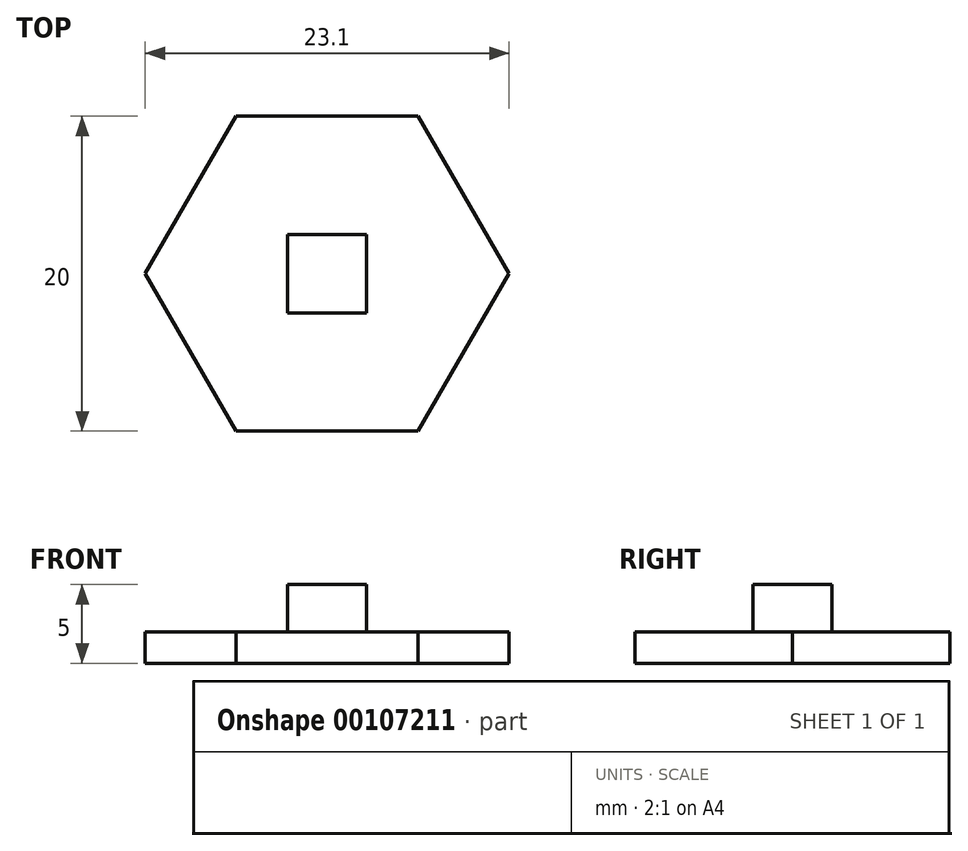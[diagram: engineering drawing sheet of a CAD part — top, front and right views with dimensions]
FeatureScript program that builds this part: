
annotation { "Feature Type Name" : "Feature", "Feature Type Description" : "" }
export const myFeature = defineFeature(function(context is Context, id is Id, definition is map)
    precondition{}
    {
        {
            var Q0;
            Q0=qCreatedBy(makeId("Top.planeOp"),FACE);
            var sketch = newSketch(context, id + "F0", { "sketchPlane" : qUnion([Q0])});
            skCircle(sketch, "E0.cCircle", {"center": v(0, 0) * mm, "radius": 10 * mm, "construction": true});
            skLineSegment(sketch, "E0.0", {"start": v(-5.77, 10) * mm, "end": v(5.77, 10) * mm});
            skLineSegment(sketch, "E0.1", {"start": v(5.77, 10) * mm, "end": v(11.55, 0) * mm});
            skLineSegment(sketch, "E0.2", {"start": v(11.55, 0) * mm, "end": v(5.77, -10) * mm});
            skLineSegment(sketch, "E0.3", {"start": v(5.77, -10) * mm, "end": v(-5.77, -10) * mm});
            skLineSegment(sketch, "E0.4", {"start": v(-5.77, -10) * mm, "end": v(-11.55, 0) * mm});
            skLineSegment(sketch, "E0.5", {"start": v(-11.55, 0) * mm, "end": v(-5.77, 10) * mm});
            skPoint(sketch, "E0.0.midPoint", {"position": v(0, 10) * mm});
            skSolve(sketch);
        }
        {
            var Q0;
            Q0=makeQuery(id+"F0.imprint","IMPRINT",FACE,{"disambiguationData":[TD([[makeQuery(id+"F0.imprint","IMPRINT",EDGE,{"derivedFrom":sQuery(id+"F0.wireOp",EDGE,"E0.0")}),-1.0]])]});
            extrude(context, id + "F1", {"entities" : qUnion([Q0]), "depth" : 2 * mm});
        }
        {
            var Q0;
            Q0=makeQuery(id+"F1.opExtrude","CAP_FACE",FACE,{"disambiguationData":[OSD([sQuery(id+"F0.wireOp",EDGE,"E0.0"),sQuery(id+"F0.wireOp",EDGE,"E0.1"),sQuery(id+"F0.wireOp",EDGE,"E0.2"),sQuery(id+"F0.wireOp",EDGE,"E0.3"),sQuery(id+"F0.wireOp",EDGE,"E0.4"),sQuery(id+"F0.wireOp",EDGE,"E0.5")])],"isStart":false});
            var sketch = newSketch(context, id + "F2", { "sketchPlane" : qUnion([Q0])});
            skLineSegment(sketch, "E1.bottom", {"start": v(-2.5, 2.5) * mm, "end": v(2.5, 2.5) * mm});
            skLineSegment(sketch, "E1.top", {"start": v(-2.5, -2.5) * mm, "end": v(2.5, -2.5) * mm});
            skLineSegment(sketch, "E1.left", {"start": v(-2.5, 2.5) * mm, "end": v(-2.5, -2.5) * mm});
            skLineSegment(sketch, "E1.right", {"start": v(2.5, 2.5) * mm, "end": v(2.5, -2.5) * mm});
            skLineSegment(sketch, "E2", {"start": v(0, 0) * mm, "end": v(0, 2.5) * mm, "construction": true});
            skLineSegment(sketch, "E3", {"start": v(2.5, 0) * mm, "end": v(0, 0) * mm, "construction": true});
            skSolve(sketch);
        }
        {
            var Q0;
            Q0=makeQuery(id+"F2.imprint","IMPRINT",FACE,{"disambiguationData":[TD([[makeQuery(id+"F2.imprint","IMPRINT",EDGE,{"derivedFrom":sQuery(id+"F2.wireOp",EDGE,"E1.bottom")}),-1.0]])]});
            extrude(context, id + "F3", {"entities" : qUnion([Q0]), "operationType" : NewBodyOperationType.ADD, "depth" : 3 * mm});
        }
    });
